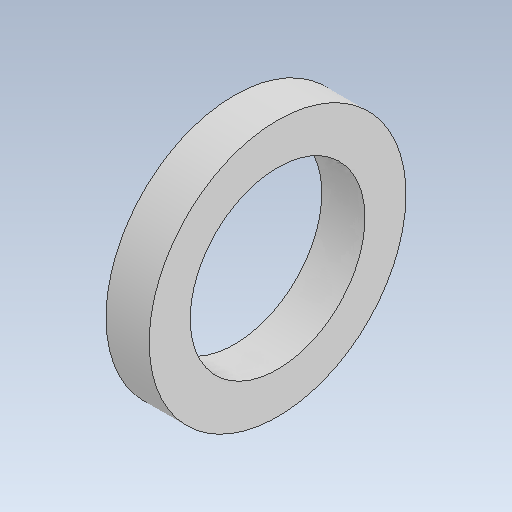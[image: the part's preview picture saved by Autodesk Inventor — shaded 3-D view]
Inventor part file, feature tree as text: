
AUTODESK INVENTOR PART (.ipt)
format: ipt  version: 2021 (Build 250183000, 183)  size: 105,984 bytes
history: native  units: mm
features: extrude x1, sketch x1
ambient origin geometry x8: Origin, YZ Plane, XZ Plane, XY Plane, X Axis, Y Axis, Z Axis, Center Point
bodies: Solid1 (feature_tree)
feature tree (2):
  extrude  "Extrusion1"  Depth=10.0mm
  sketch  "Sketch1"  dims[d0=40.5mm d1=9.5mm d2=10.0mm d3=0.0mm]
